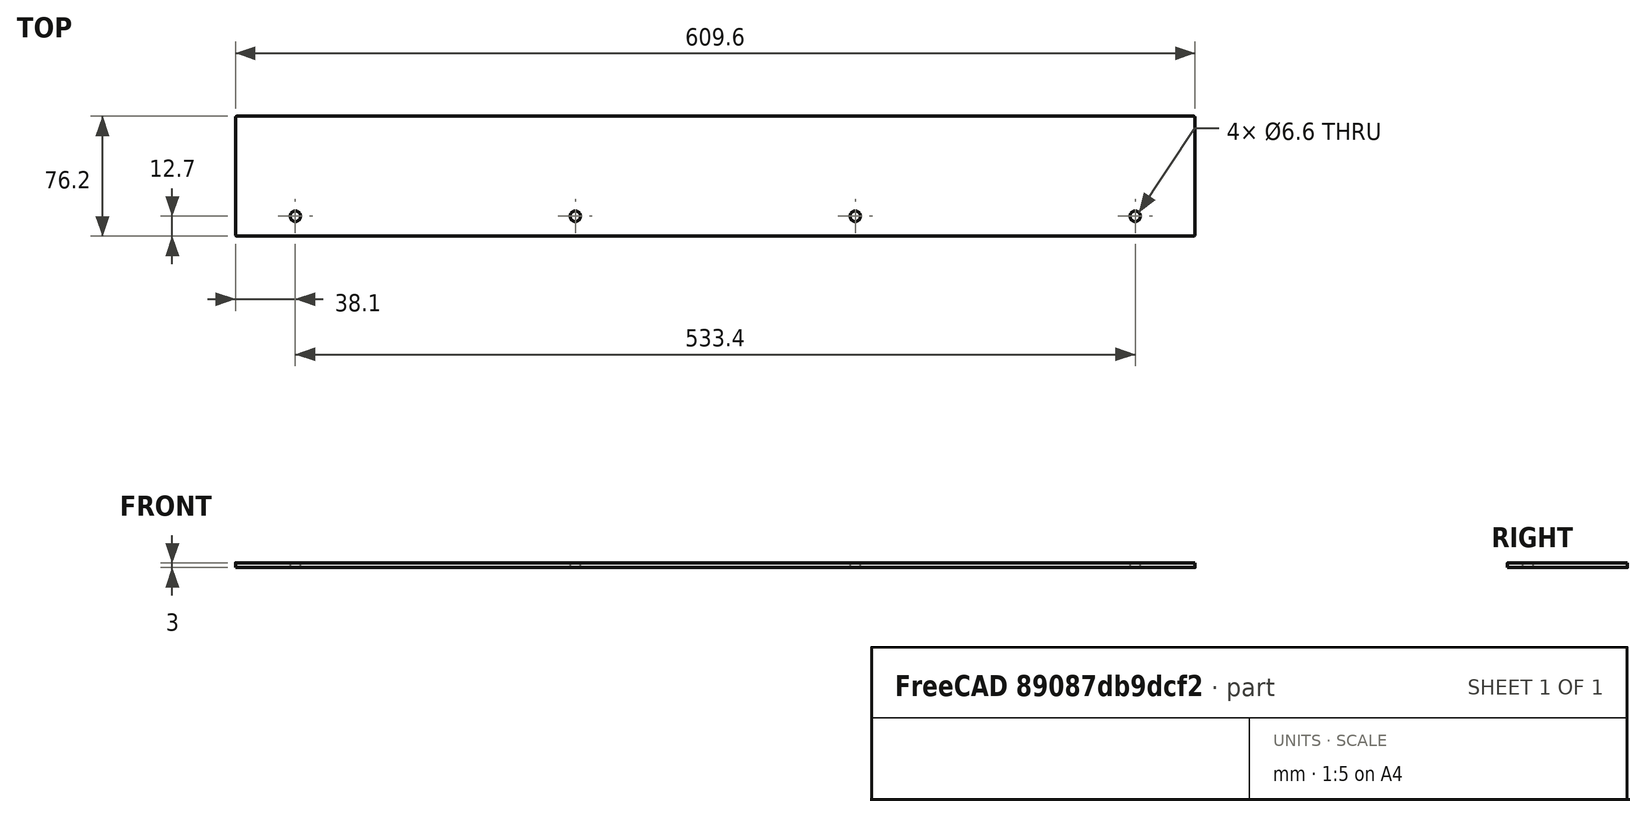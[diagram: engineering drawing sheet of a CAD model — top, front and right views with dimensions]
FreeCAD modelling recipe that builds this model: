
FCSTD DOCUMENT  (FreeCAD 0.20R29603 (Git))
Label: left_wall_24in
License: All rights reserved
LicenseURL: http://en.wikipedia.org/wiki/All_rights_reserved
objects: Sketcher::SketchObject×1, Spreadsheet::Sheet×1, PartDesign::Pad×1, PartDesign::Body×1
note: 4 computed .brp shape members not serialized (recipe doc carries the construction recipe); baked Part::Feature solids carry a one-line shape summary decoded from their .brp

FEATURE [Sketcher::SketchObject] Sketch
  FullyConstrained = true
  MapMode = 5
  Support = -> [XY_Plane]
  expr: Constraints[19] = Spreadsheet.FilletRadius
  expr: Constraints[21] = Spreadsheet.Height
  expr: Constraints[22] = Spreadsheet.Length
  expr: Constraints[34] = Spreadsheet.MountHoleSpacing
  expr: Constraints[35] = Spreadsheet.MountHoleDistanceFromBottom
  expr: Constraints[43] = Spreadsheet.MountHoleDiameter
  sketch-geometry (18):
    g0: ArcOfCircle CenterX=-303.8 CenterY=37.1 CenterZ=0 NormalX=0 NormalY=0 NormalZ=1 AngleXU=0 Radius=1 StartAngle=1.5708 EndAngle=3.14159
    g1: LineSegment StartX=-303.8 StartY=38.1 StartZ=0 EndX=303.8 EndY=38.1 EndZ=0
    g2: ArcOfCircle CenterX=303.8 CenterY=37.1 CenterZ=0 NormalX=0 NormalY=0 NormalZ=1 AngleXU=0 Radius=1 StartAngle=2.5e-15 EndAngle=1.5708
    g3: LineSegment StartX=304.8 StartY=37.1 StartZ=0 EndX=304.8 EndY=-37.1 EndZ=0
    g4: ArcOfCircle CenterX=303.8 CenterY=-37.1 CenterZ=0 NormalX=0 NormalY=0 NormalZ=1 AngleXU=0 Radius=1 StartAngle=4.71239 EndAngle=6.28319
    g5: LineSegment StartX=303.8 StartY=-38.1 StartZ=0 EndX=-303.8 EndY=-38.1 EndZ=0
    g6: ArcOfCircle CenterX=-303.8 CenterY=-37.1 CenterZ=0 NormalX=0 NormalY=0 NormalZ=1 AngleXU=0 Radius=1 StartAngle=3.14159 EndAngle=4.71239
    g7: LineSegment StartX=-304.8 StartY=-37.1 StartZ=0 EndX=-304.8 EndY=37.1 EndZ=0
    g8: GeomPoint X=-304.8 Y=38.1 Z=0
    g9: GeomPoint X=304.8 Y=-38.1 Z=0
    g10: LineSegment StartX=-266.7 StartY=-25.4 StartZ=0 EndX=-88.9 EndY=-25.4 EndZ=0
    g11: LineSegment StartX=-88.9 StartY=-25.4 StartZ=0 EndX=88.9 EndY=-25.4 EndZ=0
    g12: LineSegment StartX=88.9 StartY=-25.4 StartZ=0 EndX=266.7 EndY=-25.4 EndZ=0
    g13: LineSegment StartX=-4e-16 StartY=-38.1 StartZ=0 EndX=-4e-16 EndY=-25.4 EndZ=0
    g14: Circle CenterX=-266.7 CenterY=-25.4 CenterZ=0 NormalX=0 NormalY=0 NormalZ=1 AngleXU=0 Radius=3.302
    g15: Circle CenterX=-88.9 CenterY=-25.4 CenterZ=0 NormalX=0 NormalY=0 NormalZ=1 AngleXU=0 Radius=3.302
    g16: Circle CenterX=88.9 CenterY=-25.4 CenterZ=0 NormalX=0 NormalY=0 NormalZ=1 AngleXU=0 Radius=3.302
    g17: Circle CenterX=266.7 CenterY=-25.4 CenterZ=0 NormalX=0 NormalY=0 NormalZ=1 AngleXU=0 Radius=3.302
  constraints (44):
    c: Tangent(g0,g1) = 1.5708
    c: Tangent(g1,g2) = 1.5708
    c: Tangent(g2,g3) = 1.5708
    c: Tangent(g3,g4) = 1.5708
    c: Tangent(g4,g5) = 1.5708
    c: Tangent(g5,g6) = 1.5708
    c: Tangent(g6,g7) = 1.5708
    c: Tangent(g7,g0) = 1.5708
    c: Horizontal(g1)
    c: Horizontal(g5)
    c: Vertical(g3)
    c: Vertical(g7)
    c: Equal(g0,g2)
    c: Equal(g2,g4)
    c: Equal(g4,g6)
    c: PointOnObject(g8,g1)
    c: PointOnObject(g8,g7)
    c: PointOnObject(g9,g3)
    c: PointOnObject(g9,g5)
    c: Radius(g2) = 1
    c: Symmetric(g8,g9,g-1)
    c: DistanceY(g4,g1) = 76.2
    c: DistanceX(g0,g2) = 609.6
    c: Horizontal(g10)
    c: Coincident(g10,g11)
    c: Horizontal(g11)
    c: Coincident(g11,g12)
    c: Horizontal(g12)
    c: Equal(g10,g11)
    c: Equal(g11,g12)
    c: Vertical(g13)
    c: PointOnObject(g13,g5)
    c: PointOnObject(g13,g-2)
    c: Symmetric(g10,g11,g13)
    c: DistanceX(g11,g11) = 177.8
    c: DistanceY(g13,g13) = 12.7
    c: Coincident(g14,g10)
    c: Coincident(g15,g10)
    c: Coincident(g16,g11)
    c: Coincident(g17,g12)
    c: Equal(g14,g15)
    c: Equal(g14,g16)
    c: Equal(g14,g17)
    c: Diameter(g14) = 6.604
FEATURE [Spreadsheet::Sheet] Spreadsheet
  cells = A2=Parameters; A3=Height; B3(Height)==3in; A4=Length; B4(Length)==24in; A5=Thickness; B5(Thickness)==3mm; A6=FilletRadius; B6(FilletRadius)==1mm; A7=MountHoleDiameter; B7(MountHoleDiameter)==0.26in; A8=MountHoleDistanceFromBottom; B8(MountHoleDistanceFromBottom)==0.5in; A9=MountHoleSpacing; B9(MountHoleSpacing)==7in
FEATURE [PartDesign::Pad] Pad
  Direction = (0,0,1)
  Length = 3
  Length2 = 10
  Profile = -> Sketch
  ReferenceAxis = -> Sketch [N_Axis]
  Type = 0
  expr: Length = Spreadsheet.Thickness
FEATURE [PartDesign::Body] Body
  Group = -> [Sketch,Pad]
  Origin = -> Origin
  Tip = -> Pad
